# Revit family: C8600
name_source: partatom
category: Specialty Equipment
units: mm (PartAtom-declared; Revit-internal decimal feet)

## family parameters
Always vertical = No
Cut with Voids When Loaded = No
Maintain Annotation Orientation = No
Part Type = Normal
Room Calculation Point = No
Round Connector Dimension = Use Diameter
Shared = No
Work Plane-Based = Yes

## types (1)
- C8600 Faucet
    Cold Water Consumption = 24 GPM
    Cold Water Flow Rate = 24 GPM
    Cold Water Inlet Flow = 24 GPM
    Cold Water Maximum Pressure = 125.00 psi
    Cold Water Minimum Pressure = 20.00 psi
    Cold Water Size = 1"
    Cold water Temerature Recommended = 40 °F
    Default Elevation = 48"
    Description = Hand Sink
    Faucet Material = Lead Free Brass
    Manufacturer = Krome USA Inc.
    Maximum Temperature = 140 °F
    Minimum Teperature = 40 °F
    Model = C8600
    Product Name = Single Pantry Faucet, Single Hole Base, Wall Mount, 8 1/2" Swivel gooseneck
    URL = https://www.aluids.com
    Water Supply Radius = 1/2"

## geometry (parser evidence)
native form markers: Sweep x3
no freeform markers — native parametric forms only
